# Revit family: Pasacables
name_source: partatom
category: Aparatos eléctricos
revit_build: Autodesk Revit 2016 (Build: 20150220_1215(x64)
units: mm (PartAtom-declared; Revit-internal decimal feet)

## family parameters
Anfitrión = Cara
Compartido = No
Corte con vacíos al cargar = No
Cota de conector redondo = Diámetro de uso
Mantener orientación de anotación = No
Número OmniClass = 23.80.50.11.11
Punto de cálculo de habitación = No
Tipo de pieza = Normal
Título OmniClass = Receptacle Terminal Units

## types (3) — shared parameters
Capacidad = 5 módulos 45x45
Compatibilidad = Gama 45
Composición = Marco, Anclajes (2ud), Tapa giratoria
Código de montaje = D5020100
Descripción = Pasacables empotrado
Elevación por defecto = 1200 mm
Fabricante = MMCONECTA
Instalación = Empotrado en suelo técnico
Materia prima = Policarbonato libre de halógenos
Modelo = Pasacables P108
P108 (AltoxLargoxAncho) = 49 x - x Ø107 mm
P127 (AltoxLargoxAncho) = 49 x - x Ø127 mm
P60 (AltoxLargoxAncho) = 25 x - x Ø60 mm
P80 (AltoxLargoxAncho) = 25 x - x Ø80 mm
URL = http://www.mmconecta.com

## per-type parameters (varying)
| type | Acabado |
| Módulo /4 - Blanco | Blanco nieve RAL9019 |
| Módulo /6 - Grafito | Grafito RAL7021 |
| Módulo /8 - Gris | Gris RAL7011 |

## geometry (parser evidence)
native form markers: Blend x4
no freeform markers — native parametric forms only
